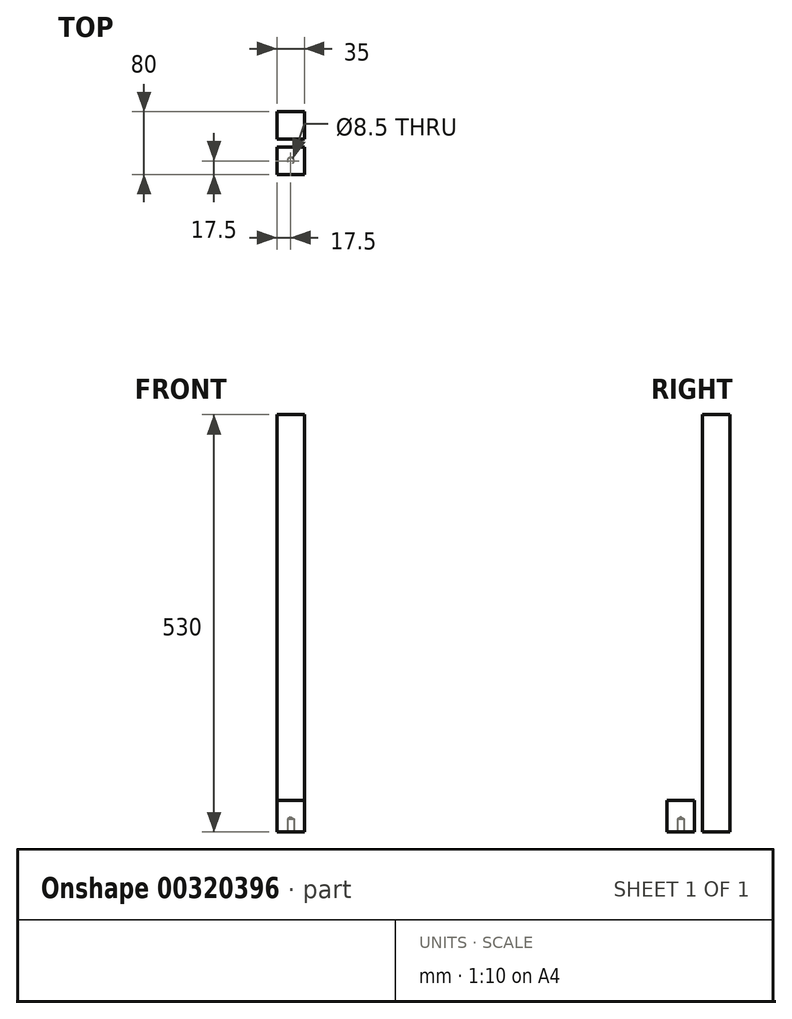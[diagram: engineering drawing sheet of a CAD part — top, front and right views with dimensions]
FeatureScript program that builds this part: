
annotation { "Feature Type Name" : "Feature", "Feature Type Description" : "" }
export const myFeature = defineFeature(function(context is Context, id is Id, definition is map)
    precondition{}
    {
        {
            assignVariable(context, id + "F0", {"name" : "Beinlaenge", "anyValue" : 40});
        }
        {
            var Q0;
            Q0=qCreatedBy(makeId("Top.planeOp"),FACE);
            var sketch = newSketch(context, id + "F1", { "sketchPlane" : qUnion([Q0])});
            skLineSegment(sketch, "E0.bottom", {"start": v(0, 0) * mm, "end": v(35, 0) * mm});
            skLineSegment(sketch, "E0.top", {"start": v(0, -35) * mm, "end": v(35, -35) * mm});
            skLineSegment(sketch, "E0.left", {"start": v(0, 0) * mm, "end": v(0, -35) * mm});
            skLineSegment(sketch, "E0.right", {"start": v(35, 0) * mm, "end": v(35, -35) * mm});
            skSolve(sketch);
        }
        {
            var Q0;
            Q0=makeQuery(id+"F1.imprint","IMPRINT",FACE,{"disambiguationData":[TD([[makeQuery(id+"F1.imprint","IMPRINT",EDGE,{"derivedFrom":sQuery(id+"F1.wireOp",EDGE,"E0.bottom")}),-1.0]])]});
            extrude(context, id + "F2", {"entities" : qUnion([Q0]), "depth" : (getVariable(context, 'Beinlaenge')) * mm});
        }
        {
            var Q0;
            Q0 = qSketchRegion(id + "F1", true);
            extrude(context, id + "F3", {"entities" : qUnion([Q0]), "depth" : 530 * mm});
        }
        {
            var Q0;
            Q0=makeQuery(id+"F3.opExtrude","SWEPT_BODY",BODY,{"disambiguationData":[OSD([sQuery(id+"F1.wireOp",EDGE,"E0.bottom"),sQuery(id+"F1.wireOp",EDGE,"E0.top"),sQuery(id+"F1.wireOp",EDGE,"E0.left"),sQuery(id+"F1.wireOp",EDGE,"E0.right")])]});
            transform(context, id + "F4", {"entities" : qUnion([Q0]), "transformType" : TransformType.TRANSLATION_3D, "dx" : 0 * mm, "dy" : 45 * mm, "dz" : 0 * mm, "makeCopy" : false});
        }
        {
            var Q0;
            Q0=makeQuery(id+"F2.opExtrude","CAP_FACE",FACE,{"disambiguationData":[OSD([sQuery(id+"F1.wireOp",EDGE,"E0.bottom"),sQuery(id+"F1.wireOp",EDGE,"E0.top"),sQuery(id+"F1.wireOp",EDGE,"E0.left"),sQuery(id+"F1.wireOp",EDGE,"E0.right")])],"isStart":true});
            var sketch = newSketch(context, id + "F5", { "sketchPlane" : qUnion([Q0])});
            skCircle(sketch, "E1", {"center": v(17.5, 17.5) * mm, "radius": 5 * mm});
            skPoint(sketch, "E1.centerSnap0", {"position": v(35, 17.5) * mm});
            skPoint(sketch, "E1.centerSnap1", {"position": v(17.5, 0) * mm});
            skSolve(sketch);
        }
        {
            var Q0;
            Q0=sQuery(id+"F5.wireOp",VERTEX,"E1.center");
            var Q1;
            Q1=makeQuery(id+"F2.opExtrude","SWEPT_BODY",BODY,{"disambiguationData":[OSD([sQuery(id+"F1.wireOp",EDGE,"E0.bottom"),sQuery(id+"F1.wireOp",EDGE,"E0.top"),sQuery(id+"F1.wireOp",EDGE,"E0.left"),sQuery(id+"F1.wireOp",EDGE,"E0.right")])]});
            hole(context, id + "F6", {"style" : HoleStyle.SIMPLE, "endStyle" : HoleEndStyle.BLIND, "standardTappedOrClearance" : lookupTablePath({ "standard" : "ISO", "engagement" : "75%", "pitch" : "1.5 mm", "size" : "M10", "type" : "Tapped" }), "standardBlindInLast" : lookupTablePath({ "standard" : "ISO", "engagement" : "75%", "pitch" : "1.5 mm", "size" : "M10", "type" : "Tapped" }), "holeDiameter" : 8.5 * mm, "showTappedDepth" : true, "holeDepth" : 16.5 * mm, "tappedDepth" : 12 * mm, "tapClearance" : 3, "locations" : qUnion([Q0]), "scope" : qUnion([Q1]), "majorDiameter" : 10 * mm});
        }
    });
